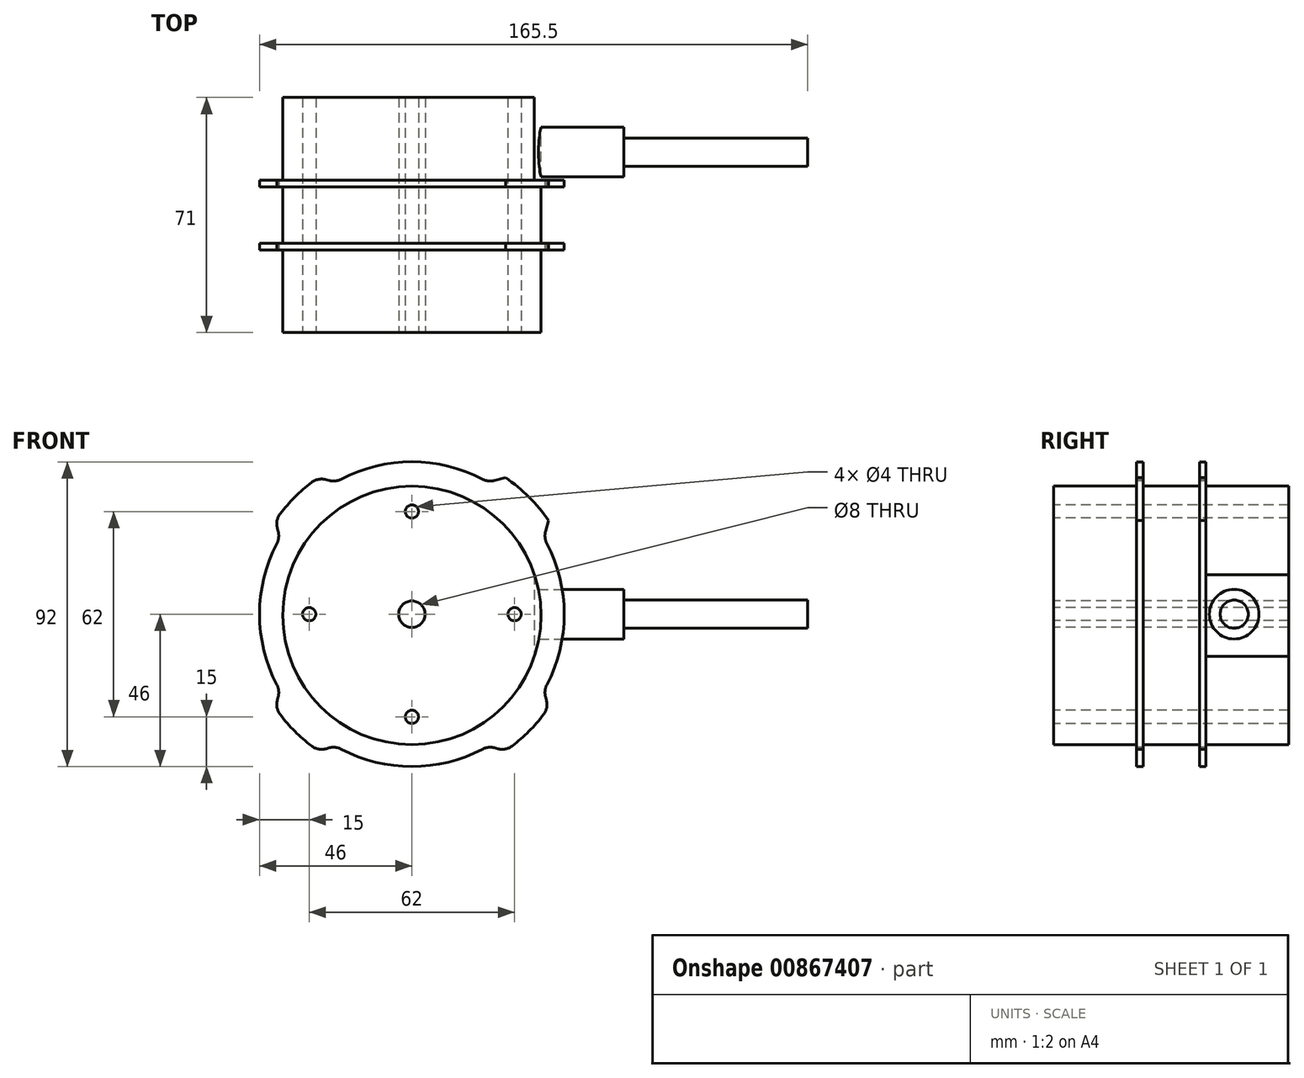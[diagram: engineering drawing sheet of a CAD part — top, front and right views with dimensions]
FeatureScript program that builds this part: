
annotation { "Feature Type Name" : "Feature", "Feature Type Description" : "" }
export const myFeature = defineFeature(function(context is Context, id is Id, definition is map)
    precondition{}
    {
        {
            var Q0;
            Q0=qCreatedBy(makeId("Front.planeOp"),FACE);
            var sketch = newSketch(context, id + "F0", { "sketchPlane" : qUnion([Q0])});
            skCircle(sketch, "E0", {"center": v(0, 0) * mm, "radius": 50 * mm});
            skSolve(sketch);
        }
        {
            var Q0;
            Q0=qSketchRegion(id+"F0",true);
            extrude(context, id + "F1", {"entities" : qUnion([Q0]), "endBound" : BoundingType.SYMMETRIC, "depth" : 21 * mm, "offsetDistance" : 25 * mm});
        }
        {
            var Q0;
            Q0=qCreatedBy(makeId("Front.planeOp"),FACE);
            var sketch = newSketch(context, id + "F2", { "sketchPlane" : qUnion([Q0])});
            skCircle(sketch, "E1.0", {"center": v(0, 0) * mm, "radius": 50 * mm});
            skSolve(sketch);
        }
        {
            var Q0;
            Q0=qSketchRegion(id+"F2",true);
            extrude(context, id + "F3", {"entities" : qUnion([Q0]), "operationType" : NewBodyOperationType.REMOVE, "endBound" : BoundingType.SYMMETRIC, "oppositeDirection" : true, "depth" : 17 * mm, "offsetDistance" : 25 * mm});
        }
        {
            var Q0;
            Q0=qCreatedBy(makeId("Front.planeOp"),FACE);
            var sketch = newSketch(context, id + "F4", { "sketchPlane" : qUnion([Q0])});
            skCircle(sketch, "E2", {"center": v(0, -0.36) * mm, "radius": 39 * mm});
            skSolve(sketch);
        }
        {
            var Q0;
            Q0=qSketchRegion(id+"F4",true);
            extrude(context, id + "F5", {"entities" : qUnion([Q0]), "endBound" : BoundingType.SYMMETRIC, "depth" : 71 * mm, "offsetDistance" : 25 * mm});
        }
        {
            var Q0;
            Q0=qCreatedBy(makeId("Front.planeOp"),FACE);
            var sketch = newSketch(context, id + "F6", { "sketchPlane" : qUnion([Q0])});
            skCircle(sketch, "E3", {"center": v(0, 0) * mm, "radius": 46 * mm});
            skCircle(sketch, "E4.0", {"center": v(0, 0) * mm, "radius": 50 * mm});
            skLineSegment(sketch, "E5", {"start": v(0, 0) * mm, "end": v(-50, 0) * mm, "construction": true});
            skLineSegment(sketch, "E6", {"start": v(-50, 0) * mm, "end": v(50, 0) * mm, "construction": true});
            skLineSegment(sketch, "E7", {"start": v(0, -50) * mm, "end": v(0, 50) * mm, "construction": true});
            skLineSegment(sketch, "E8", {"start": v(-25, 43.3) * mm, "end": v(25, -43.3) * mm, "construction": true});
            skLineSegment(sketch, "E9", {"start": v(-43.3, 25) * mm, "end": v(43.3, -25) * mm, "construction": true});
            skLineSegment(sketch, "E10", {"start": v(-23, 39.84) * mm, "end": v(-28.26, 41.25) * mm});
            skLineSegment(sketch, "E11", {"start": v(-39.84, 23) * mm, "end": v(-41.25, 28.26) * mm});
            skLineSegment(sketch, "E12.MirrorCS", {"start": v(23, 39.84) * mm, "end": v(28.26, 41.25) * mm});
            skLineSegment(sketch, "E13.MirrorCS", {"start": v(39.84, 23) * mm, "end": v(41.25, 28.26) * mm});
            skLineSegment(sketch, "E14.MirrorCS", {"start": v(-43.3, -25) * mm, "end": v(43.3, 25) * mm, "construction": true});
            skLineSegment(sketch, "E15.MirrorCS", {"start": v(-23, -39.84) * mm, "end": v(-28.26, -41.25) * mm});
            skLineSegment(sketch, "E16.MirrorCS", {"start": v(23, -39.84) * mm, "end": v(28.26, -41.25) * mm});
            skLineSegment(sketch, "E17.MirrorCS", {"start": v(39.84, -23) * mm, "end": v(41.25, -28.26) * mm});
            skLineSegment(sketch, "E18.MirrorCS", {"start": v(-39.84, -23) * mm, "end": v(-41.25, -28.26) * mm});
            skSolve(sketch);
        }
        {
            var Q0;
            {var subQ0=sQuery(id+"F6.wireOp",EDGE,"E10");Q0=makeQuery(id+"F6.imprint","IMPRINT",FACE,{"disambiguationData":[TD([[makeQuery(id+"F6.imprint","IMPRINT",EDGE,{"derivedFrom":subQ0}),-1.0]])]});}
            var Q1;
            {var subQ0=sQuery(id+"F6.wireOp",EDGE,"E16.MirrorCS");Q1=makeQuery(id+"F6.imprint","IMPRINT",FACE,{"disambiguationData":[TD([[makeQuery(id+"F6.imprint","IMPRINT",EDGE,{"derivedFrom":subQ0}),-1.0]])]});}
            var Q2;
            {var subQ0=sQuery(id+"F6.wireOp",EDGE,"E11");Q2=makeQuery(id+"F6.imprint","IMPRINT",FACE,{"disambiguationData":[TD([[makeQuery(id+"F6.imprint","IMPRINT",EDGE,{"derivedFrom":subQ0}),1.0]])]});}
            var Q3;
            {var subQ0=sQuery(id+"F6.wireOp",EDGE,"E13.MirrorCS");Q3=makeQuery(id+"F6.imprint","IMPRINT",FACE,{"disambiguationData":[TD([[makeQuery(id+"F6.imprint","IMPRINT",EDGE,{"derivedFrom":subQ0}),-1.0]])]});}
            extrude(context, id + "F7", {"entities" : qUnion([Q0, Q1, Q2, Q3]), "operationType" : NewBodyOperationType.REMOVE, "endBound" : BoundingType.SYMMETRIC, "oppositeDirection" : true, "depth" : 25 * mm, "offsetDistance" : 25 * mm});
        }
        {
            var Q0;
            {var subQ0=sQuery(id+"F6.wireOp",EDGE,"E3");var subQ1=sQuery(id+"F6.wireOp",EDGE,"E10");Q0=makeQuery(id+"F7.boolean.opBoolean","COPY",EDGE,{"disambiguationData":[TD([makeQuery(id+"F1.opExtrude","CAP_FACE",FACE,{"disambiguationData":[OSD([sQuery(id+"F0.wireOp",EDGE,"E0")])],"isStart":false})])],"derivedFrom":makeQuery(id+"F7.opExtrude","SWEPT_EDGE",EDGE,{"disambiguationData":[OSD([subQ0,subQ1])]})});}
            var Q1;
            {var subQ0=sQuery(id+"F6.wireOp",EDGE,"E3");var subQ1=sQuery(id+"F6.wireOp",EDGE,"E10");Q1=makeQuery(id+"F7.boolean.opBoolean","COPY",EDGE,{"disambiguationData":[TD([makeQuery(id+"F1.opExtrude","CAP_FACE",FACE,{"disambiguationData":[OSD([sQuery(id+"F0.wireOp",EDGE,"E0")])],"isStart":true})])],"derivedFrom":makeQuery(id+"F7.opExtrude","SWEPT_EDGE",EDGE,{"disambiguationData":[OSD([subQ0,subQ1])]})});}
            var Q2;
            {var subQ0=sQuery(id+"F0.wireOp",EDGE,"E0");var subQ1=sQuery(id+"F6.wireOp",EDGE,"E10");Q2=makeQuery(id+"F7.boolean.opBoolean","COPY",EDGE,{"disambiguationData":[TD([makeQuery(id+"F1.opExtrude","CAP_FACE",FACE,{"disambiguationData":[OSD([subQ0])],"isStart":true})])],"derivedFrom":makeQuery(id+"F7.opExtrude","SWEPT_EDGE",EDGE,{"disambiguationData":[OSD([sQuery(id+"F6.wireOp",EDGE,"E4.0"),subQ1])]})});}
            var Q3;
            {var subQ0=sQuery(id+"F0.wireOp",EDGE,"E0");var subQ1=sQuery(id+"F6.wireOp",EDGE,"E10");Q3=makeQuery(id+"F7.boolean.opBoolean","COPY",EDGE,{"disambiguationData":[TD([makeQuery(id+"F1.opExtrude","CAP_FACE",FACE,{"disambiguationData":[OSD([subQ0])],"isStart":false})])],"derivedFrom":makeQuery(id+"F7.opExtrude","SWEPT_EDGE",EDGE,{"disambiguationData":[OSD([sQuery(id+"F6.wireOp",EDGE,"E4.0"),subQ1])]})});}
            var Q4;
            {var subQ0=sQuery(id+"F0.wireOp",EDGE,"E0");var subQ1=sQuery(id+"F6.wireOp",EDGE,"E11");Q4=makeQuery(id+"F7.boolean.opBoolean","COPY",EDGE,{"disambiguationData":[TD([makeQuery(id+"F1.opExtrude","CAP_FACE",FACE,{"disambiguationData":[OSD([subQ0])],"isStart":false})])],"derivedFrom":makeQuery(id+"F7.opExtrude","SWEPT_EDGE",EDGE,{"disambiguationData":[OSD([sQuery(id+"F6.wireOp",EDGE,"E4.0"),subQ1])]})});}
            var Q5;
            {var subQ0=sQuery(id+"F6.wireOp",EDGE,"E3");var subQ1=sQuery(id+"F6.wireOp",EDGE,"E11");Q5=makeQuery(id+"F7.boolean.opBoolean","COPY",EDGE,{"disambiguationData":[TD([makeQuery(id+"F1.opExtrude","CAP_FACE",FACE,{"disambiguationData":[OSD([sQuery(id+"F0.wireOp",EDGE,"E0")])],"isStart":false})])],"derivedFrom":makeQuery(id+"F7.opExtrude","SWEPT_EDGE",EDGE,{"disambiguationData":[OSD([subQ0,subQ1])]})});}
            var Q6;
            {var subQ0=sQuery(id+"F6.wireOp",EDGE,"E3");var subQ1=sQuery(id+"F6.wireOp",EDGE,"E11");Q6=makeQuery(id+"F7.boolean.opBoolean","COPY",EDGE,{"disambiguationData":[TD([makeQuery(id+"F1.opExtrude","CAP_FACE",FACE,{"disambiguationData":[OSD([sQuery(id+"F0.wireOp",EDGE,"E0")])],"isStart":true})])],"derivedFrom":makeQuery(id+"F7.opExtrude","SWEPT_EDGE",EDGE,{"disambiguationData":[OSD([subQ0,subQ1])]})});}
            var Q7;
            {var subQ0=sQuery(id+"F0.wireOp",EDGE,"E0");var subQ1=sQuery(id+"F6.wireOp",EDGE,"E11");Q7=makeQuery(id+"F7.boolean.opBoolean","COPY",EDGE,{"disambiguationData":[TD([makeQuery(id+"F1.opExtrude","CAP_FACE",FACE,{"disambiguationData":[OSD([subQ0])],"isStart":true})])],"derivedFrom":makeQuery(id+"F7.opExtrude","SWEPT_EDGE",EDGE,{"disambiguationData":[OSD([sQuery(id+"F6.wireOp",EDGE,"E4.0"),subQ1])]})});}
            var Q8;
            {var subQ0=sQuery(id+"F6.wireOp",EDGE,"E3");var subQ1=sQuery(id+"F6.wireOp",EDGE,"E12.MirrorCS");Q8=makeQuery(id+"F7.boolean.opBoolean","COPY",EDGE,{"disambiguationData":[TD([makeQuery(id+"F1.opExtrude","CAP_FACE",FACE,{"disambiguationData":[OSD([sQuery(id+"F0.wireOp",EDGE,"E0")])],"isStart":true})])],"derivedFrom":makeQuery(id+"F7.opExtrude","SWEPT_EDGE",EDGE,{"disambiguationData":[OSD([subQ0,subQ1])]})});}
            var Q9;
            {var subQ0=sQuery(id+"F0.wireOp",EDGE,"E0");var subQ1=sQuery(id+"F6.wireOp",EDGE,"E12.MirrorCS");Q9=makeQuery(id+"F7.boolean.opBoolean","COPY",EDGE,{"disambiguationData":[TD([makeQuery(id+"F1.opExtrude","CAP_FACE",FACE,{"disambiguationData":[OSD([subQ0])],"isStart":true})])],"derivedFrom":makeQuery(id+"F7.opExtrude","SWEPT_EDGE",EDGE,{"disambiguationData":[OSD([sQuery(id+"F6.wireOp",EDGE,"E4.0"),subQ1])]})});}
            var Q10;
            {var subQ0=sQuery(id+"F6.wireOp",EDGE,"E3");var subQ1=sQuery(id+"F6.wireOp",EDGE,"E12.MirrorCS");Q10=makeQuery(id+"F7.boolean.opBoolean","COPY",EDGE,{"disambiguationData":[TD([makeQuery(id+"F1.opExtrude","CAP_FACE",FACE,{"disambiguationData":[OSD([sQuery(id+"F0.wireOp",EDGE,"E0")])],"isStart":false})])],"derivedFrom":makeQuery(id+"F7.opExtrude","SWEPT_EDGE",EDGE,{"disambiguationData":[OSD([subQ0,subQ1])]})});}
            var Q11;
            {var subQ0=sQuery(id+"F0.wireOp",EDGE,"E0");var subQ1=sQuery(id+"F6.wireOp",EDGE,"E12.MirrorCS");Q11=makeQuery(id+"F7.boolean.opBoolean","COPY",EDGE,{"disambiguationData":[TD([makeQuery(id+"F1.opExtrude","CAP_FACE",FACE,{"disambiguationData":[OSD([subQ0])],"isStart":false})])],"derivedFrom":makeQuery(id+"F7.opExtrude","SWEPT_EDGE",EDGE,{"disambiguationData":[OSD([sQuery(id+"F6.wireOp",EDGE,"E4.0"),subQ1])]})});}
            var Q12;
            {var subQ0=sQuery(id+"F6.wireOp",EDGE,"E13.MirrorCS");var subQ1=sQuery(id+"F6.wireOp",EDGE,"E3");Q12=makeQuery(id+"F7.boolean.opBoolean","COPY",EDGE,{"disambiguationData":[TD([makeQuery(id+"F1.opExtrude","CAP_FACE",FACE,{"disambiguationData":[OSD([sQuery(id+"F0.wireOp",EDGE,"E0")])],"isStart":true})])],"derivedFrom":makeQuery(id+"F7.opExtrude","SWEPT_EDGE",EDGE,{"disambiguationData":[OSD([subQ1,subQ0])]})});}
            var Q13;
            {var subQ0=sQuery(id+"F0.wireOp",EDGE,"E0");var subQ1=sQuery(id+"F6.wireOp",EDGE,"E13.MirrorCS");Q13=makeQuery(id+"F7.boolean.opBoolean","COPY",EDGE,{"disambiguationData":[TD([makeQuery(id+"F1.opExtrude","CAP_FACE",FACE,{"disambiguationData":[OSD([subQ0])],"isStart":true})])],"derivedFrom":makeQuery(id+"F7.opExtrude","SWEPT_EDGE",EDGE,{"disambiguationData":[OSD([sQuery(id+"F6.wireOp",EDGE,"E4.0"),subQ1])]})});}
            var Q14;
            {var subQ0=sQuery(id+"F0.wireOp",EDGE,"E0");var subQ1=sQuery(id+"F6.wireOp",EDGE,"E13.MirrorCS");Q14=makeQuery(id+"F7.boolean.opBoolean","COPY",EDGE,{"disambiguationData":[TD([makeQuery(id+"F1.opExtrude","CAP_FACE",FACE,{"disambiguationData":[OSD([subQ0])],"isStart":false})])],"derivedFrom":makeQuery(id+"F7.opExtrude","SWEPT_EDGE",EDGE,{"disambiguationData":[OSD([sQuery(id+"F6.wireOp",EDGE,"E4.0"),subQ1])]})});}
            var Q15;
            {var subQ0=sQuery(id+"F6.wireOp",EDGE,"E13.MirrorCS");var subQ1=sQuery(id+"F6.wireOp",EDGE,"E3");Q15=makeQuery(id+"F7.boolean.opBoolean","COPY",EDGE,{"disambiguationData":[TD([makeQuery(id+"F1.opExtrude","CAP_FACE",FACE,{"disambiguationData":[OSD([sQuery(id+"F0.wireOp",EDGE,"E0")])],"isStart":false})])],"derivedFrom":makeQuery(id+"F7.opExtrude","SWEPT_EDGE",EDGE,{"disambiguationData":[OSD([subQ1,subQ0])]})});}
            var Q16;
            {var subQ0=sQuery(id+"F6.wireOp",EDGE,"E17.MirrorCS");var subQ1=sQuery(id+"F6.wireOp",EDGE,"E3");Q16=makeQuery(id+"F7.boolean.opBoolean","COPY",EDGE,{"disambiguationData":[TD([makeQuery(id+"F1.opExtrude","CAP_FACE",FACE,{"disambiguationData":[OSD([sQuery(id+"F0.wireOp",EDGE,"E0")])],"isStart":true})])],"derivedFrom":makeQuery(id+"F7.opExtrude","SWEPT_EDGE",EDGE,{"disambiguationData":[OSD([subQ1,subQ0])]})});}
            var Q17;
            {var subQ0=sQuery(id+"F0.wireOp",EDGE,"E0");var subQ1=sQuery(id+"F6.wireOp",EDGE,"E17.MirrorCS");Q17=makeQuery(id+"F7.boolean.opBoolean","COPY",EDGE,{"disambiguationData":[TD([makeQuery(id+"F1.opExtrude","CAP_FACE",FACE,{"disambiguationData":[OSD([subQ0])],"isStart":true})])],"derivedFrom":makeQuery(id+"F7.opExtrude","SWEPT_EDGE",EDGE,{"disambiguationData":[OSD([sQuery(id+"F6.wireOp",EDGE,"E4.0"),subQ1])]})});}
            var Q18;
            {var subQ0=sQuery(id+"F6.wireOp",EDGE,"E3");var subQ1=sQuery(id+"F6.wireOp",EDGE,"E17.MirrorCS");Q18=makeQuery(id+"F7.boolean.opBoolean","COPY",EDGE,{"disambiguationData":[TD([makeQuery(id+"F1.opExtrude","CAP_FACE",FACE,{"disambiguationData":[OSD([sQuery(id+"F0.wireOp",EDGE,"E0")])],"isStart":false})])],"derivedFrom":makeQuery(id+"F7.opExtrude","SWEPT_EDGE",EDGE,{"disambiguationData":[OSD([subQ0,subQ1])]})});}
            var Q19;
            {var subQ0=sQuery(id+"F0.wireOp",EDGE,"E0");var subQ1=sQuery(id+"F6.wireOp",EDGE,"E17.MirrorCS");Q19=makeQuery(id+"F7.boolean.opBoolean","COPY",EDGE,{"disambiguationData":[TD([makeQuery(id+"F1.opExtrude","CAP_FACE",FACE,{"disambiguationData":[OSD([subQ0])],"isStart":false})])],"derivedFrom":makeQuery(id+"F7.opExtrude","SWEPT_EDGE",EDGE,{"disambiguationData":[OSD([sQuery(id+"F6.wireOp",EDGE,"E4.0"),subQ1])]})});}
            var Q20;
            {var subQ0=sQuery(id+"F0.wireOp",EDGE,"E0");var subQ1=sQuery(id+"F6.wireOp",EDGE,"E16.MirrorCS");Q20=makeQuery(id+"F7.boolean.opBoolean","COPY",EDGE,{"disambiguationData":[TD([makeQuery(id+"F1.opExtrude","CAP_FACE",FACE,{"disambiguationData":[OSD([subQ0])],"isStart":true})])],"derivedFrom":makeQuery(id+"F7.opExtrude","SWEPT_EDGE",EDGE,{"disambiguationData":[OSD([sQuery(id+"F6.wireOp",EDGE,"E4.0"),subQ1])]})});}
            var Q21;
            {var subQ0=sQuery(id+"F6.wireOp",EDGE,"E16.MirrorCS");var subQ1=sQuery(id+"F6.wireOp",EDGE,"E3");Q21=makeQuery(id+"F7.boolean.opBoolean","COPY",EDGE,{"disambiguationData":[TD([makeQuery(id+"F1.opExtrude","CAP_FACE",FACE,{"disambiguationData":[OSD([sQuery(id+"F0.wireOp",EDGE,"E0")])],"isStart":true})])],"derivedFrom":makeQuery(id+"F7.opExtrude","SWEPT_EDGE",EDGE,{"disambiguationData":[OSD([subQ1,subQ0])]})});}
            var Q22;
            {var subQ0=sQuery(id+"F0.wireOp",EDGE,"E0");var subQ1=sQuery(id+"F6.wireOp",EDGE,"E16.MirrorCS");Q22=makeQuery(id+"F7.boolean.opBoolean","COPY",EDGE,{"disambiguationData":[TD([makeQuery(id+"F1.opExtrude","CAP_FACE",FACE,{"disambiguationData":[OSD([subQ0])],"isStart":false})])],"derivedFrom":makeQuery(id+"F7.opExtrude","SWEPT_EDGE",EDGE,{"disambiguationData":[OSD([sQuery(id+"F6.wireOp",EDGE,"E4.0"),subQ1])]})});}
            var Q23;
            {var subQ0=sQuery(id+"F6.wireOp",EDGE,"E16.MirrorCS");var subQ1=sQuery(id+"F6.wireOp",EDGE,"E3");Q23=makeQuery(id+"F7.boolean.opBoolean","COPY",EDGE,{"disambiguationData":[TD([makeQuery(id+"F1.opExtrude","CAP_FACE",FACE,{"disambiguationData":[OSD([sQuery(id+"F0.wireOp",EDGE,"E0")])],"isStart":false})])],"derivedFrom":makeQuery(id+"F7.opExtrude","SWEPT_EDGE",EDGE,{"disambiguationData":[OSD([subQ1,subQ0])]})});}
            var Q24;
            {var subQ0=sQuery(id+"F6.wireOp",EDGE,"E15.MirrorCS");var subQ1=sQuery(id+"F6.wireOp",EDGE,"E3");Q24=makeQuery(id+"F7.boolean.opBoolean","COPY",EDGE,{"disambiguationData":[TD([makeQuery(id+"F1.opExtrude","CAP_FACE",FACE,{"disambiguationData":[OSD([sQuery(id+"F0.wireOp",EDGE,"E0")])],"isStart":false})])],"derivedFrom":makeQuery(id+"F7.opExtrude","SWEPT_EDGE",EDGE,{"disambiguationData":[OSD([subQ1,subQ0])]})});}
            var Q25;
            {var subQ0=sQuery(id+"F6.wireOp",EDGE,"E3");var subQ1=sQuery(id+"F6.wireOp",EDGE,"E15.MirrorCS");Q25=makeQuery(id+"F7.boolean.opBoolean","COPY",EDGE,{"disambiguationData":[TD([makeQuery(id+"F1.opExtrude","CAP_FACE",FACE,{"disambiguationData":[OSD([sQuery(id+"F0.wireOp",EDGE,"E0")])],"isStart":true})])],"derivedFrom":makeQuery(id+"F7.opExtrude","SWEPT_EDGE",EDGE,{"disambiguationData":[OSD([subQ0,subQ1])]})});}
            var Q26;
            {var subQ0=sQuery(id+"F0.wireOp",EDGE,"E0");var subQ1=sQuery(id+"F6.wireOp",EDGE,"E15.MirrorCS");Q26=makeQuery(id+"F7.boolean.opBoolean","COPY",EDGE,{"disambiguationData":[TD([makeQuery(id+"F1.opExtrude","CAP_FACE",FACE,{"disambiguationData":[OSD([subQ0])],"isStart":true})])],"derivedFrom":makeQuery(id+"F7.opExtrude","SWEPT_EDGE",EDGE,{"disambiguationData":[OSD([sQuery(id+"F6.wireOp",EDGE,"E4.0"),subQ1])]})});}
            var Q27;
            {var subQ0=sQuery(id+"F0.wireOp",EDGE,"E0");var subQ1=sQuery(id+"F6.wireOp",EDGE,"E15.MirrorCS");Q27=makeQuery(id+"F7.boolean.opBoolean","COPY",EDGE,{"disambiguationData":[TD([makeQuery(id+"F1.opExtrude","CAP_FACE",FACE,{"disambiguationData":[OSD([subQ0])],"isStart":false})])],"derivedFrom":makeQuery(id+"F7.opExtrude","SWEPT_EDGE",EDGE,{"disambiguationData":[OSD([sQuery(id+"F6.wireOp",EDGE,"E4.0"),subQ1])]})});}
            var Q28;
            {var subQ0=sQuery(id+"F6.wireOp",EDGE,"E3");var subQ1=sQuery(id+"F6.wireOp",EDGE,"E18.MirrorCS");Q28=makeQuery(id+"F7.boolean.opBoolean","COPY",EDGE,{"disambiguationData":[TD([makeQuery(id+"F1.opExtrude","CAP_FACE",FACE,{"disambiguationData":[OSD([sQuery(id+"F0.wireOp",EDGE,"E0")])],"isStart":true})])],"derivedFrom":makeQuery(id+"F7.opExtrude","SWEPT_EDGE",EDGE,{"disambiguationData":[OSD([subQ0,subQ1])]})});}
            var Q29;
            {var subQ0=sQuery(id+"F0.wireOp",EDGE,"E0");var subQ1=sQuery(id+"F6.wireOp",EDGE,"E18.MirrorCS");Q29=makeQuery(id+"F7.boolean.opBoolean","COPY",EDGE,{"disambiguationData":[TD([makeQuery(id+"F1.opExtrude","CAP_FACE",FACE,{"disambiguationData":[OSD([subQ0])],"isStart":true})])],"derivedFrom":makeQuery(id+"F7.opExtrude","SWEPT_EDGE",EDGE,{"disambiguationData":[OSD([sQuery(id+"F6.wireOp",EDGE,"E4.0"),subQ1])]})});}
            var Q30;
            {var subQ0=sQuery(id+"F0.wireOp",EDGE,"E0");var subQ1=sQuery(id+"F6.wireOp",EDGE,"E18.MirrorCS");Q30=makeQuery(id+"F7.boolean.opBoolean","COPY",EDGE,{"disambiguationData":[TD([makeQuery(id+"F1.opExtrude","CAP_FACE",FACE,{"disambiguationData":[OSD([subQ0])],"isStart":false})])],"derivedFrom":makeQuery(id+"F7.opExtrude","SWEPT_EDGE",EDGE,{"disambiguationData":[OSD([sQuery(id+"F6.wireOp",EDGE,"E4.0"),subQ1])]})});}
            var Q31;
            {var subQ0=sQuery(id+"F6.wireOp",EDGE,"E3");var subQ1=sQuery(id+"F6.wireOp",EDGE,"E18.MirrorCS");Q31=makeQuery(id+"F7.boolean.opBoolean","COPY",EDGE,{"disambiguationData":[TD([makeQuery(id+"F1.opExtrude","CAP_FACE",FACE,{"disambiguationData":[OSD([sQuery(id+"F0.wireOp",EDGE,"E0")])],"isStart":false})])],"derivedFrom":makeQuery(id+"F7.opExtrude","SWEPT_EDGE",EDGE,{"disambiguationData":[OSD([subQ0,subQ1])]})});}
            fillet(context, id + "F8", {"entities" : qUnion([Q0, Q1, Q2, Q3, Q4, Q5, Q6, Q7, Q8, Q9, Q10, Q11, Q12, Q13, Q14, Q15, Q16, Q17, Q18, Q19, Q20, Q21, Q22, Q23, Q24, Q25, Q26, Q27, Q28, Q29, Q30, Q31]), "radius" : 5 * mm, "tangentPropagation" : true, "allowEdgeOverflow" : false});
        }
        {
            var Q0;
            Q0=makeQuery(id+"F5.opExtrude","CAP_FACE",FACE,{"disambiguationData":[OSD([sQuery(id+"F4.wireOp",EDGE,"E2")])],"isStart":false});
            var sketch = newSketch(context, id + "F9", { "sketchPlane" : qUnion([Q0])});
            skCircle(sketch, "E19", {"center": v(0, 31) * mm, "radius": 2 * mm});
            skCircle(sketch, "E20", {"center": v(0, 0) * mm, "radius": 31 * mm, "construction": true});
            skCircle(sketch, "E21", {"center": v(-31, 0) * mm, "radius": 2 * mm});
            skCircle(sketch, "E22", {"center": v(31, 0) * mm, "radius": 2 * mm});
            skCircle(sketch, "E23", {"center": v(0, -31) * mm, "radius": 2 * mm});
            skSolve(sketch);
        }
        {
            var Q0;
            Q0=qSketchRegion(id+"F9",true);
            extrude(context, id + "F10", {"entities" : qUnion([Q0]), "operationType" : NewBodyOperationType.REMOVE, "endBound" : BoundingType.THROUGH_ALL, "oppositeDirection" : true, "depth" : 25 * mm, "offsetDistance" : 25 * mm});
        }
        {
            var Q0;
            Q0=qCreatedBy(makeId("Front.planeOp"),FACE);
            var sketch = newSketch(context, id + "F11", { "sketchPlane" : qUnion([Q0])});
            skCircle(sketch, "E24", {"center": v(0, 0) * mm, "radius": 4 * mm});
            skSolve(sketch);
        }
        {
            var Q0;
            Q0=qSketchRegion(id+"F11",true);
            extrude(context, id + "F12", {"entities" : qUnion([Q0]), "depth" : 25 * mm, "offsetDistance" : 25 * mm});
        }
        {
            var Q0;
            Q0=qSketchRegion(id+"F11",true);
            var Q1;
            Q1=makeQuery(id+"F5.opExtrude","CAP_FACE",FACE,{"disambiguationData":[OSD([sQuery(id+"F4.wireOp",EDGE,"E2")])],"isStart":false});
            var Q2;
            Q2=makeQuery(id+"F5.opExtrude","CAP_FACE",FACE,{"disambiguationData":[OSD([sQuery(id+"F4.wireOp",EDGE,"E2")])],"isStart":true});
            extrude(context, id + "F13", {"entities" : qUnion([Q0]), "operationType" : NewBodyOperationType.REMOVE, "endBound" : BoundingType.UP_TO_NEXT, "oppositeDirection" : true, "depth" : 25 * mm, "endBoundEntityFace" : qUnion([Q1]), "offsetDistance" : 25 * mm, "hasSecondDirection" : true, "secondDirectionBound" : SecondDirectionBoundingType.UP_TO_NEXT, "secondDirectionOppositeDirection" : false, "secondDirectionDepth" : 25 * mm, "secondDirectionBoundEntityFace" : qUnion([Q2])});
        }
        {
            var Q0;
            Q0=qSketchRegion(id+"F11",true);
            var Q1;
            Q1=makeQuery(id+"F5.opExtrude","CAP_FACE",FACE,{"disambiguationData":[OSD([sQuery(id+"F4.wireOp",EDGE,"E2")])],"isStart":true});
            var Q2;
            Q2=makeQuery(id+"F5.opExtrude","CAP_FACE",FACE,{"disambiguationData":[OSD([sQuery(id+"F4.wireOp",EDGE,"E2")])],"isStart":false});
            extrude(context, id + "F14", {"entities" : qUnion([Q0]), "operationType" : NewBodyOperationType.REMOVE, "endBound" : BoundingType.UP_TO_SURFACE, "oppositeDirection" : true, "depth" : 25 * mm, "endBoundEntityFace" : qUnion([Q1]), "offsetDistance" : 25 * mm, "hasSecondDirection" : true, "secondDirectionBound" : SecondDirectionBoundingType.UP_TO_SURFACE, "secondDirectionOppositeDirection" : false, "secondDirectionDepth" : 25 * mm, "secondDirectionBoundEntityFace" : qUnion([Q2])});
        }
        {
            var Q0;
            Q0=makeQuery(id+"F3.boolean.opBoolean","SPLIT",BODY,{"disambiguationData":[OD(0.0)],"derivedFrom":makeQuery(id+"F1.opExtrude","SWEPT_BODY",BODY,{"disambiguationData":[OSD([sQuery(id+"F0.wireOp",EDGE,"E0")])]})});
            var Q1;
            Q1=makeQuery(id+"F3.boolean.opBoolean","SPLIT",BODY,{"disambiguationData":[OD(1.0)],"derivedFrom":makeQuery(id+"F1.opExtrude","SWEPT_BODY",BODY,{"disambiguationData":[OSD([sQuery(id+"F0.wireOp",EDGE,"E0")])]})});
            var Q2;
            Q2=makeQuery(id+"F5.opExtrude","SWEPT_BODY",BODY,{"disambiguationData":[OSD([sQuery(id+"F4.wireOp",EDGE,"E2")])]});
            booleanBodies(context, id + "F15", {"operationType" : BooleanOperationType.UNION, "tools" : qUnion([Q0, Q1, Q2])});
        }
        {
            var Q0;
            Q0=qCreatedBy(makeId("Right.planeOp"),FACE);
            cPlane(context, id + "F16", {"entities" : qUnion([Q0]), "cplaneType" : CPlaneType.OFFSET, "offset" : 39 * mm, "width" : 150 * mm, "height" : 150 * mm});
        }
        {
            var Q0;
            Q0=qCreatedBy(id+"F16.planeOp",FACE);
            var sketch = newSketch(context, id + "F17", { "sketchPlane" : qUnion([Q0])});
            skCircle(sketch, "E25", {"center": v(19, 0) * mm, "radius": 7.5 * mm});
            skLineSegment(sketch, "E26.0", {"start": v(10.5, -21.33) * mm, "end": v(10.5, 21.33) * mm, "construction": true});
            skSolve(sketch);
        }
        {
            var Q0;
            Q0=qSketchRegion(id+"F17",true);
            extrude(context, id + "F18", {"entities" : qUnion([Q0]), "oppositeDirection" : true, "depth" : 2 * mm, "offsetDistance" : 25 * mm, "hasSecondDirection" : true, "secondDirectionOppositeDirection" : false, "secondDirectionDepth" : 25 * mm});
        }
        {
            var Q0;
            Q0=makeQuery(id+"F18.opExtrude","CAP_FACE",FACE,{"disambiguationData":[OSD([sQuery(id+"F17.wireOp",EDGE,"E25")])],"isStart":true});
            var sketch = newSketch(context, id + "F19", { "sketchPlane" : qUnion([Q0])});
            skCircle(sketch, "E27", {"center": v(19, 0) * mm, "radius": 4.25 * mm});
            skSolve(sketch);
        }
        {
            var Q0;
            Q0=qSketchRegion(id+"F19",true);
            extrude(context, id + "F20", {"entities" : qUnion([Q0]), "operationType" : NewBodyOperationType.ADD, "depth" : 55.5 * mm, "offsetDistance" : 25 * mm});
        }
        {
            var Q0;
            Q0=makeQuery(id+"F5.opExtrude","CAP_FACE",FACE,{"disambiguationData":[OSD([sQuery(id+"F4.wireOp",EDGE,"E2")])],"isStart":true});
            var sketch = newSketch(context, id + "F21", { "sketchPlane" : qUnion([Q0])});
            skCircle(sketch, "E28.0", {"center": v(0, -0.36) * mm, "radius": 39 * mm});
            skLineSegment(sketch, "E29", {"start": v(-37, 11.96) * mm, "end": v(-37, -12.7) * mm});
            skSolve(sketch);
        }
        {
            var Q0;
            {var subQ0=sQuery(id+"F21.wireOp",EDGE,"E29");Q0=makeQuery(id+"F21.imprint","IMPRINT",FACE,{"disambiguationData":[TD([[makeQuery(id+"F21.imprint","IMPRINT",EDGE,{"derivedFrom":subQ0}),-1.0]])]});}
            var Q1;
            Q1=makeQuery(id+"F1.opExtrude","CAP_FACE",FACE,{"disambiguationData":[OSD([sQuery(id+"F0.wireOp",EDGE,"E0")])],"isStart":true});
            extrude(context, id + "F22", {"entities" : qUnion([Q0]), "operationType" : NewBodyOperationType.REMOVE, "endBound" : BoundingType.UP_TO_SURFACE, "oppositeDirection" : true, "depth" : 25 * mm, "endBoundEntityFace" : qUnion([Q1]), "offsetDistance" : 25 * mm});
        }
    });
